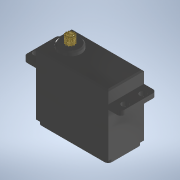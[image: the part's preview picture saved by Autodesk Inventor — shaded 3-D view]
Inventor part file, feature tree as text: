
AUTODESK INVENTOR PART (.ipt)
format: ipt  version: 2021 (Build 250183000, 183)  size: 394,752 bytes
history: native  units: mm
features: sketch x15, extrude x9, projected_geometry x9, chamfer x3, plane x3, other x3, fillet x2, pattern_circular x1, reference x1
ambient origin geometry x8: Origin, YZ Plane, XZ Plane, XY Plane, X Axis, Y Axis, Z Axis, Center Point
bodies: Solid1 (feature_tree)
feature tree (46):
  extrude  "Extrusion1"  Depth=26.67mm TaperAngle=0.0deg
  extrude  "Extrusion2"  Depth=6.85mm TaperAngle=0.0deg
  extrude  "Extrusion3"  Depth=5.0mm
  extrude  "Extrusion8"  Depth=4.05mm TaperAngle=15.0deg
  extrude  "Extrusion4"  Depth=4.05mm TaperAngle=360.0deg
  extrude  "Extrusion5"  Depth=2.0mm TaperAngle=0.0deg
  extrude  "Extrusion6"  Depth=2.0mm
  pattern_circular  "Circular Pattern1"  Count=4  [1 undecoded]
  extrude  "Extrusion7"  Depth=7.0mm
  fillet  "Fillet1"  Radius=20.0mm
  extrude  "Extrusion9"  Depth=54.0mm
  chamfer  "Chamfer1"  Distance=2.0mm
  fillet  "Fillet2"  Radius=5.0mm
  chamfer  "Chamfer2"  Distance=2.0mm Angle=45.0deg
  chamfer  "Chamfer3"  Distance=2.0mm
  sketch  "Sketch10"  dims[d50=777.0mm d51=0.0mm]
  plane  "Work Plane1"
  sketch  "Sketch13"  dims[d52=9.66mm d53=40.0mm]
  sketch  "Sketch14"  dims[d54=4.5mm d55=7.0mm d56=20.0mm]
  sketch  "Sketch16"  dims[d57=54.0mm d58=4.5mm]
  sketch  "Sketch18"  dims[d59=2.5mm]
  sketch  "Sketch19"  dims[d60=2.5mm d61=2.0mm d62=5.0mm d63=0.0mm d64=0.7mm d65=2.0mm d66=45.0deg d67=2.0mm d68=0.7mm d69=2.0mm d70=45.0deg d71=0.7mm d72=2.0mm d73=45.0deg d74=13.47mm d75=0.0mm d83=15.0deg d84=15.0deg]
  plane  "Work Plane2"
  plane  "Work Plane3"
  sketch  "Sketch1"  dims[d1=19.82mm d2=26.67mm d3=0.0mm]
  sketch  "Sketch2"  dims[d5=2.5mm d6=0.0mm d7=6.85mm d8=0.0mm]
  sketch  "Sketch3"  dims[d11=2.33mm d12=0.0mm d13=5.0mm]
  sketch  "Sketch4"  dims[d14=4.05mm d15=0.0mm d21=4.2mm d23=15.0deg]
  sketch  "Sketch5"  dims[d24=4.05mm d25=0.0mm d26=120.0mm d27=360.0deg]
  sketch  "Sketch6"  dims[d29=0.5mm d30=2.0mm d31=0.0mm]
  sketch  "Sketch7"  dims[d32=2.0mm d47=3.8mm]
  sketch  "Sketch8"  dims[d48=3.8mm]
  sketch  "Sketch9"  dims[d49=3.8mm]
  projected_geometry  "Projected Loop1"
  projected_geometry  "Projected Loop2"
  projected_geometry  "Projected Loop3"
  reference  "Reference1"
  projected_geometry  "Projected Loop7"
  projected_geometry  "Projected Loop8"
  projected_geometry  "Projected Loop9"
  projected_geometry  "Projected Loop10"
  projected_geometry  "Projected Loop13"
  projected_geometry  "Projected Loop15"
  other  "<userpath>\Documents\Inventor\tu2space\servoAssembly.iam"
  other  "servoAssembly.iam"
  other  "SERVOHORN:1"
note: 1 required parameter value undecoded (feature->parameter linkage not recoverable at this tier; creation-order binding heuristic only, values carry confidence <= 0.55)
